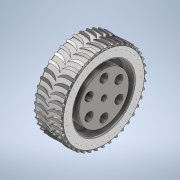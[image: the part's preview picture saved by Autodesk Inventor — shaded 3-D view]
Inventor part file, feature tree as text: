
AUTODESK INVENTOR PART (.ipt)
format: ipt  version: 2021 (Build 250183000, 183)  size: 677,376 bytes
history: native  units: mm
features: sketch x9, extrude x7, fillet x4, plane x1, pattern_circular x1
ambient origin geometry x8: Origin, YZ Plane, XZ Plane, XY Plane, X Axis, Y Axis, Z Axis, Center Point
bodies: Solid1 (feature_tree), Solid2 (feature_tree), Solid3 (feature_tree)
feature tree (22):
  extrude  "Extrusion1"  Depth=50.0mm TaperAngle=0.0deg
  fillet  "Fillet1"  Radius=2.0mm
  extrude  "Extrusion2"  Depth=90.0mm
  extrude  "Extrusion3"  Depth=110.0mm
  extrude  "Extrusion6"  Depth=20.0mm TaperAngle=0.0deg
  extrude  "Extrusion7"  Depth=60.0mm TaperAngle=360.0deg
  fillet  "Fillet2"  Radius=100.0mm
  sketch  "Sketch8"  dims[d25=10.0mm d26=100.0mm d27=0.0mm]
  sketch  "Sketch9"  dims[d28=2.0mm d29=76.5mm d30=10.0mm d31=0.0mm d32=10.0mm d33=0.0mm]
  plane  "Work Plane2"
  sketch  "Sketch10"  dims[d34=0.2mm]
  sketch  "Sketch11"  dims[d35=0.2mm d36=400.0mm d37=360.0deg d12=0.5mm d13=0.872665mm]
  extrude  "Extrusion8"  Depth=10.0mm TaperAngle=0.0deg
  extrude  "Extrusion9"  Depth=10.0mm
  fillet  "Fillet3"  Radius=10.0mm
  fillet  "Fillet4"  Radius=10.0mm
  pattern_circular  "Circular Pattern1"  Count=40 Angle=360.0deg
  sketch  "Sketch1"  dims[d0=150.0mm d1=50.0mm d2=0.0mm d3=2.0mm]
  sketch  "Sketch2"  dims[d4=110.0mm d5=90.0mm]
  sketch  "Sketch3"  dims[d6=20.0mm d7=0.0mm d8=110.0mm]
  sketch  "Sketch6"  dims[d9=95.0mm d10=20.0mm d11=0.0mm]
  sketch  "Sketch7"  dims[d18=15.0mm d19=60.0mm d21=360.0deg d23=100.0mm d24=0.0mm]
